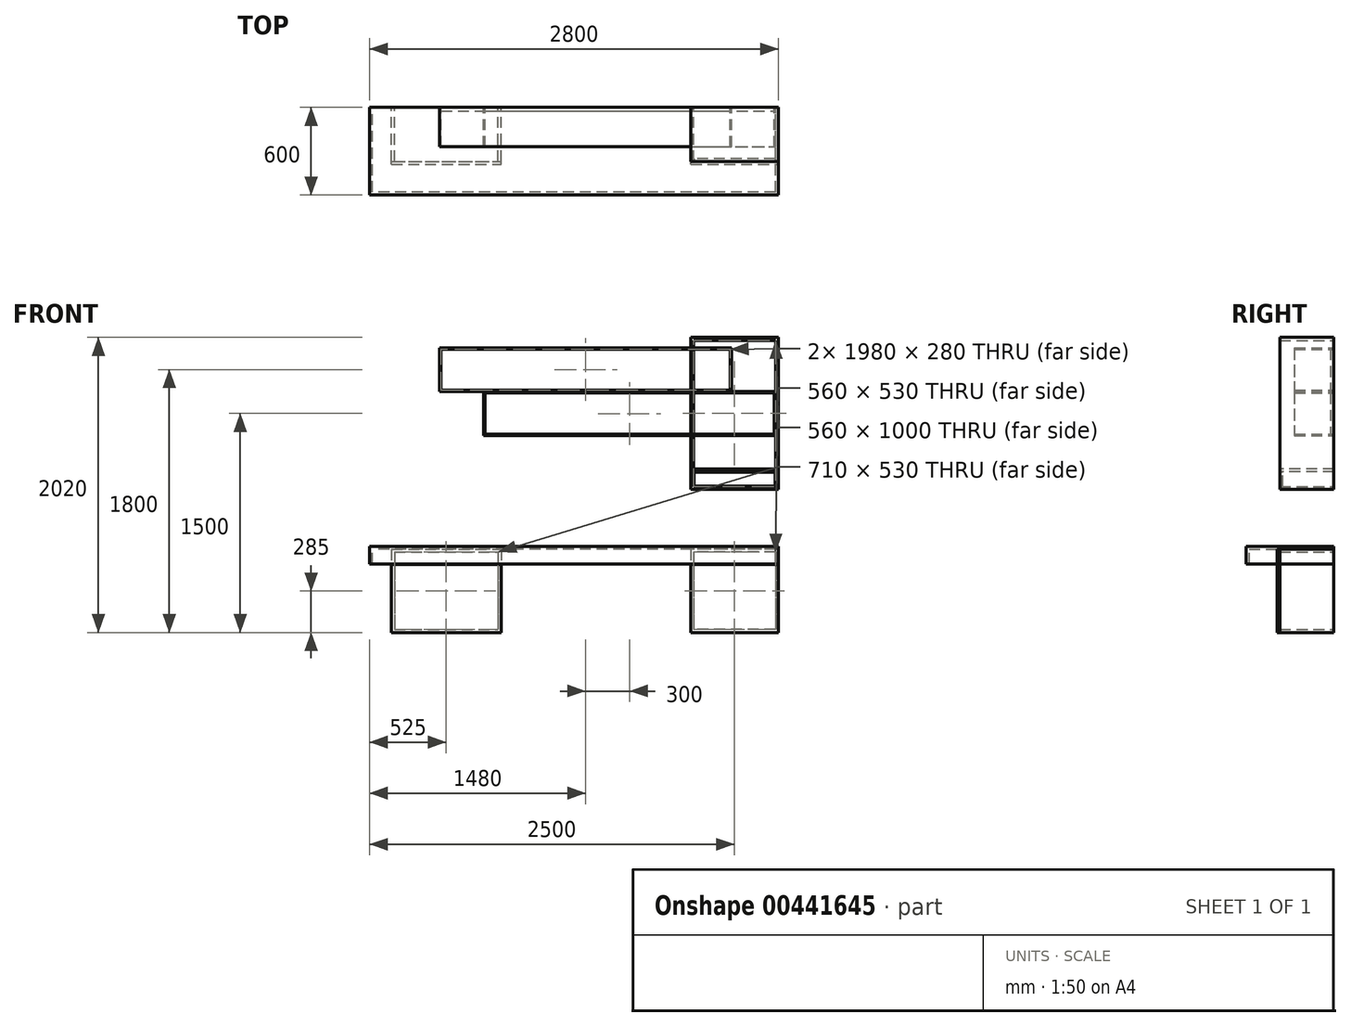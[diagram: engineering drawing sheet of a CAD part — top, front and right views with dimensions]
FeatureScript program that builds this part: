
annotation { "Feature Type Name" : "Feature", "Feature Type Description" : "" }
export const myFeature = defineFeature(function(context is Context, id is Id, definition is map)
    precondition{}
    {
        {
            var Q0;
            Q0=qCreatedBy(makeId("Front.planeOp"),FACE);
            var sketch = newSketch(context, id + "F0", { "sketchPlane" : qUnion([Q0])});
            skLineSegment(sketch, "E0.bottom", {"start": v(-1500, 2200) * mm, "end": v(1500, 2200) * mm});
            skLineSegment(sketch, "E0.top", {"start": v(-1500, 0) * mm, "end": v(1500, 0) * mm});
            skLineSegment(sketch, "E0.left", {"start": v(-1500, 2200) * mm, "end": v(-1500, 0) * mm});
            skLineSegment(sketch, "E0.right", {"start": v(1500, 2200) * mm, "end": v(1500, 0) * mm});
            skPoint(sketch, "E1", {"position": v(0, 0) * mm});
            skLineSegment(sketch, "E2.bottom", {"start": v(-1250, 770) * mm, "end": v(-500, 770) * mm});
            skLineSegment(sketch, "E2.top", {"start": v(-1250, 170) * mm, "end": v(-500, 170) * mm});
            skLineSegment(sketch, "E2.left", {"start": v(-1250, 770) * mm, "end": v(-1250, 170) * mm});
            skLineSegment(sketch, "E2.right", {"start": v(-500, 770) * mm, "end": v(-500, 170) * mm});
            skSolve(sketch);
        }
        {
            var Q0;
            Q0=qCreatedBy(makeId("Top.planeOp"),FACE);
            var Q1;
            Q1=sQuery(id+"F0.wireOp",VERTEX,"E2.left.start");
            cPlane(context, id + "F1", {"entities" : qUnion([Q0, Q1]), "cplaneType" : CPlaneType.PLANE_POINT, "offset" : 25 * mm, "width" : 150 * mm, "height" : 150 * mm});
        }
        {
            var Q0;
            Q0=qCreatedBy(id+"F1.planeOp",FACE);
            var sketch = newSketch(context, id + "F2", { "sketchPlane" : qUnion([Q0])});
            skLineSegment(sketch, "E3.bottom", {"start": v(1400, -600) * mm, "end": v(-1400, -600) * mm});
            skLineSegment(sketch, "E3.top", {"start": v(1400, 0) * mm, "end": v(-1400, 0) * mm});
            skLineSegment(sketch, "E3.left", {"start": v(1400, -600) * mm, "end": v(1400, 0) * mm});
            skLineSegment(sketch, "E3.right", {"start": v(-1400, -600) * mm, "end": v(-1400, 0) * mm});
            skPoint(sketch, "E3.middle", {"position": v(0, -300) * mm});
            skSolve(sketch);
        }
        {
            var Q0;
            Q0=qSketchRegion(id+"F2",true);
            extrude(context, id + "F3", {"entities" : qUnion([Q0]), "depth" : 20 * mm});
        }
        {
            var Q0;
            Q0=makeQuery(id+"F3.opExtrude","CAP_FACE",FACE,{"disambiguationData":[OSD([sQuery(id+"F2.wireOp",EDGE,"E3.bottom"),sQuery(id+"F2.wireOp",EDGE,"E3.top"),sQuery(id+"F2.wireOp",EDGE,"E3.left"),sQuery(id+"F2.wireOp",EDGE,"E3.right")])],"isStart":true});
            var sketch = newSketch(context, id + "F4", { "sketchPlane" : qUnion([Q0])});
            skLineSegment(sketch, "E4.0", {"start": v(-1400, 600) * mm, "end": v(-1400, 0) * mm});
            skLineSegment(sketch, "E4.1", {"start": v(1400, 600) * mm, "end": v(-1400, 600) * mm});
            skLineSegment(sketch, "E4.2", {"start": v(1400, 600) * mm, "end": v(1400, 0) * mm});
            skLineSegment(sketch, "E5.0", {"start": v(-1380, 580) * mm, "end": v(-1380, 0) * mm});
            skLineSegment(sketch, "E5.1", {"start": v(1380, 580) * mm, "end": v(-1380, 580) * mm});
            skLineSegment(sketch, "E5.2", {"start": v(1380, 580) * mm, "end": v(1380, 0) * mm});
            skLineSegment(sketch, "E6", {"start": v(-1400, 0) * mm, "end": v(-1380, 0) * mm});
            skLineSegment(sketch, "E7", {"start": v(1400, 0) * mm, "end": v(1380, 0) * mm});
            skSolve(sketch);
        }
        {
            var Q0;
            Q0=qSketchRegion(id+"F4",true);
            extrude(context, id + "F5", {"entities" : qUnion([Q0]), "operationType" : NewBodyOperationType.ADD, "depth" : 100 * mm});
        }
        {
            var Q0;
            Q0=qCreatedBy(makeId("Front.planeOp"),FACE);
            var sketch = newSketch(context, id + "F6", { "sketchPlane" : qUnion([Q0])});
            skLineSegment(sketch, "E8.bottom", {"start": v(-1250, 770) * mm, "end": v(-500, 770) * mm});
            skLineSegment(sketch, "E8.top", {"start": v(-1250, 200) * mm, "end": v(-500, 200) * mm});
            skLineSegment(sketch, "E8.left", {"start": v(-1250, 770) * mm, "end": v(-1250, 200) * mm});
            skLineSegment(sketch, "E8.right", {"start": v(-500, 770) * mm, "end": v(-500, 200) * mm});
            skLineSegment(sketch, "E9.bottom", {"start": v(1400, 770) * mm, "end": v(800, 770) * mm});
            skLineSegment(sketch, "E9.top", {"start": v(1400, 200) * mm, "end": v(800, 200) * mm});
            skLineSegment(sketch, "E9.left", {"start": v(1400, 770) * mm, "end": v(1400, 200) * mm});
            skLineSegment(sketch, "E9.right", {"start": v(800, 770) * mm, "end": v(800, 200) * mm});
            skLineSegment(sketch, "E10.0", {"start": v(1380, 750) * mm, "end": v(1380, 220) * mm});
            skLineSegment(sketch, "E10.1", {"start": v(1380, 750) * mm, "end": v(820, 750) * mm});
            skLineSegment(sketch, "E10.2", {"start": v(820, 750) * mm, "end": v(820, 220) * mm});
            skLineSegment(sketch, "E10.3", {"start": v(1380, 220) * mm, "end": v(820, 220) * mm});
            skLineSegment(sketch, "E11.0", {"start": v(-1230, 750) * mm, "end": v(-520, 750) * mm});
            skLineSegment(sketch, "E11.1", {"start": v(-1230, 750) * mm, "end": v(-1230, 220) * mm});
            skLineSegment(sketch, "E11.2", {"start": v(-1230, 220) * mm, "end": v(-520, 220) * mm});
            skLineSegment(sketch, "E11.3", {"start": v(-520, 750) * mm, "end": v(-520, 220) * mm});
            skSolve(sketch);
        }
        {
            var Q0;
            Q0=qSketchRegion(id+"F6",true);
            extrude(context, id + "F7", {"entities" : qUnion([Q0]), "depth" : 370 * mm});
        }
        {
            var Q0;
            Q0=makeQuery(id+"F7.opExtrude","CAP_FACE",FACE,{"disambiguationData":[OSD([sQuery(id+"F6.wireOp",EDGE,"E8.bottom"),sQuery(id+"F6.wireOp",EDGE,"E8.top"),sQuery(id+"F6.wireOp",EDGE,"E8.left"),sQuery(id+"F6.wireOp",EDGE,"E8.right"),sQuery(id+"F6.wireOp",EDGE,"E11.0"),sQuery(id+"F6.wireOp",EDGE,"E11.1"),sQuery(id+"F6.wireOp",EDGE,"E11.2"),sQuery(id+"F6.wireOp",EDGE,"E11.3")])],"isStart":false});
            var sketch = newSketch(context, id + "F8", { "sketchPlane" : qUnion([Q0])});
            skLineSegment(sketch, "E12.bottom", {"start": v(-1250, 770) * mm, "end": v(-500, 770) * mm});
            skLineSegment(sketch, "E12.top", {"start": v(-1250, 670) * mm, "end": v(-500, 670) * mm});
            skLineSegment(sketch, "E12.left", {"start": v(-1250, 770) * mm, "end": v(-1250, 670) * mm});
            skLineSegment(sketch, "E12.right", {"start": v(-500, 770) * mm, "end": v(-500, 670) * mm});
            skLineSegment(sketch, "E13.bottom", {"start": v(800, 770) * mm, "end": v(1400, 770) * mm});
            skLineSegment(sketch, "E13.top", {"start": v(800, 670) * mm, "end": v(1400, 670) * mm});
            skLineSegment(sketch, "E13.left", {"start": v(800, 770) * mm, "end": v(800, 670) * mm});
            skLineSegment(sketch, "E13.right", {"start": v(1400, 770) * mm, "end": v(1400, 670) * mm});
            skLineSegment(sketch, "E14.bottom", {"start": v(-1250, 667) * mm, "end": v(-500, 667) * mm});
            skLineSegment(sketch, "E14.top", {"start": v(-1250, 200) * mm, "end": v(-500, 200) * mm});
            skLineSegment(sketch, "E14.left", {"start": v(-1250, 667) * mm, "end": v(-1250, 200) * mm});
            skLineSegment(sketch, "E14.right", {"start": v(-500, 667) * mm, "end": v(-500, 200) * mm});
            skLineSegment(sketch, "E15.bottom", {"start": v(800, 667) * mm, "end": v(1400, 667) * mm});
            skLineSegment(sketch, "E15.top", {"start": v(800, 200) * mm, "end": v(1400, 200) * mm});
            skLineSegment(sketch, "E15.left", {"start": v(800, 667) * mm, "end": v(800, 200) * mm});
            skLineSegment(sketch, "E15.right", {"start": v(1400, 667) * mm, "end": v(1400, 200) * mm});
            skSolve(sketch);
        }
        {
            var Q0;
            Q0=qSketchRegion(id+"F8",true);
            extrude(context, id + "F9", {"entities" : qUnion([Q0]), "depth" : 20 * mm});
        }
        {
            var Q0;
            Q0=makeQuery(id+"F0.imprint","IMPRINT",FACE,{"disambiguationData":[TD([[makeQuery(id+"F0.imprint","IMPRINT",EDGE,{"derivedFrom":sQuery(id+"F0.wireOp",EDGE,"E0.bottom")}),-1.0]])]});
            var sketch = newSketch(context, id + "F10", { "sketchPlane" : qUnion([Q0])});
            skLineSegment(sketch, "E16.bottom", {"start": v(-920, 2150) * mm, "end": v(1080, 2150) * mm});
            skLineSegment(sketch, "E16.top", {"start": v(-920, 1850) * mm, "end": v(1080, 1850) * mm});
            skLineSegment(sketch, "E16.left", {"start": v(-920, 2150) * mm, "end": v(-920, 1850) * mm});
            skLineSegment(sketch, "E16.right", {"start": v(1080, 2150) * mm, "end": v(1080, 1850) * mm});
            skLineSegment(sketch, "E17.bottom", {"start": v(-620, 1849) * mm, "end": v(1380, 1849) * mm});
            skLineSegment(sketch, "E17.top", {"start": v(-620, 1549) * mm, "end": v(1380, 1549) * mm});
            skLineSegment(sketch, "E17.left", {"start": v(-620, 1849) * mm, "end": v(-620, 1549) * mm});
            skLineSegment(sketch, "E17.right", {"start": v(1380, 1849) * mm, "end": v(1380, 1549) * mm});
            skLineSegment(sketch, "E18.0", {"start": v(1070, 2140) * mm, "end": v(1070, 1860) * mm});
            skLineSegment(sketch, "E18.1", {"start": v(-910, 2140) * mm, "end": v(1070, 2140) * mm});
            skLineSegment(sketch, "E18.2", {"start": v(-910, 2140) * mm, "end": v(-910, 1860) * mm});
            skLineSegment(sketch, "E18.3", {"start": v(-910, 1860) * mm, "end": v(1070, 1860) * mm});
            skLineSegment(sketch, "E19.0", {"start": v(1370, 1839) * mm, "end": v(1370, 1559) * mm});
            skLineSegment(sketch, "E19.1", {"start": v(-610, 1839) * mm, "end": v(1370, 1839) * mm});
            skLineSegment(sketch, "E19.2", {"start": v(-610, 1839) * mm, "end": v(-610, 1559) * mm});
            skLineSegment(sketch, "E19.3", {"start": v(-610, 1559) * mm, "end": v(1370, 1559) * mm});
            skSolve(sketch);
        }
        {
            var Q0;
            Q0=qSketchRegion(id+"F10",true);
            extrude(context, id + "F11", {"entities" : qUnion([Q0]), "depth" : 270 * mm});
        }
        {
            var Q0;
            Q0=qCreatedBy(makeId("Front.planeOp"),FACE);
            var sketch = newSketch(context, id + "F12", { "sketchPlane" : qUnion([Q0])});
            skLineSegment(sketch, "E20.0", {"start": v(-910, 2140) * mm, "end": v(-910, 1860) * mm});
            skLineSegment(sketch, "E20.1", {"start": v(-910, 2140) * mm, "end": v(1070, 2140) * mm});
            skLineSegment(sketch, "E20.2", {"start": v(1070, 2140) * mm, "end": v(1070, 1860) * mm});
            skLineSegment(sketch, "E20.3", {"start": v(-910, 1860) * mm, "end": v(1070, 1860) * mm});
            skLineSegment(sketch, "E21.0", {"start": v(-610, 1839) * mm, "end": v(-610, 1559) * mm});
            skLineSegment(sketch, "E21.1", {"start": v(-610, 1839) * mm, "end": v(1370, 1839) * mm});
            skLineSegment(sketch, "E21.2", {"start": v(1370, 1839) * mm, "end": v(1370, 1559) * mm});
            skLineSegment(sketch, "E21.3", {"start": v(-610, 1559) * mm, "end": v(1370, 1559) * mm});
            skSolve(sketch);
        }
        {
            var Q0;
            Q0=qSketchRegion(id+"F12",true);
            extrude(context, id + "F13", {"entities" : qUnion([Q0]), "depth" : 25 * mm});
        }
        {
            var Q0;
            Q0=qCreatedBy(makeId("Front.planeOp"),FACE);
            var sketch = newSketch(context, id + "F14", { "sketchPlane" : qUnion([Q0])});
            skLineSegment(sketch, "E22.bottom", {"start": v(1380, 1200) * mm, "end": v(820, 1200) * mm});
            skLineSegment(sketch, "E22.top", {"start": v(1380, 2200) * mm, "end": v(820, 2200) * mm});
            skLineSegment(sketch, "E22.left", {"start": v(1380, 1200) * mm, "end": v(1380, 2200) * mm});
            skLineSegment(sketch, "E22.right", {"start": v(820, 1200) * mm, "end": v(820, 2200) * mm});
            skLineSegment(sketch, "E23.0", {"start": v(1400, 1180) * mm, "end": v(800, 1180) * mm});
            skLineSegment(sketch, "E23.1", {"start": v(1400, 1180) * mm, "end": v(1400, 2220) * mm});
            skLineSegment(sketch, "E23.2", {"start": v(1400, 2220) * mm, "end": v(800, 2220) * mm});
            skLineSegment(sketch, "E23.3", {"start": v(800, 1180) * mm, "end": v(800, 2220) * mm});
            skSolve(sketch);
        }
        {
            var Q0;
            Q0=qSketchRegion(id+"F14",true);
            extrude(context, id + "F15", {"entities" : qUnion([Q0]), "depth" : 370 * mm});
        }
        {
            var Q0;
            Q0=makeQuery(id+"F15.opExtrude","SWEPT_FACE",FACE,{"disambiguationData":[OSD([sQuery(id+"F14.wireOp",EDGE,"E22.right")])]});
            var sketch = newSketch(context, id + "F16", { "sketchPlane" : qUnion([Q0])});
            skLineSegment(sketch, "E24.bottom", {"start": v(-370, 1320) * mm, "end": v(0, 1320) * mm});
            skLineSegment(sketch, "E24.top", {"start": v(-370, 1300) * mm, "end": v(0, 1300) * mm});
            skLineSegment(sketch, "E24.left", {"start": v(-370, 1320) * mm, "end": v(-370, 1300) * mm});
            skLineSegment(sketch, "E24.right", {"start": v(0, 1320) * mm, "end": v(0, 1300) * mm});
            skSolve(sketch);
        }
        {
            var Q0;
            Q0=qSketchRegion(id+"F16",true);
            extrude(context, id + "F17", {"entities" : qUnion([Q0]), "endBound" : BoundingType.UP_TO_NEXT, "depth" : 25 * mm});
        }
        {
            var Q0;
            Q0=makeQuery(id+"F17.opExtrude","SWEPT_FACE",FACE,{"disambiguationData":[OSD([sQuery(id+"F16.wireOp",EDGE,"E24.left")])]});
            var sketch = newSketch(context, id + "F18", { "sketchPlane" : qUnion([Q0])});
            skLineSegment(sketch, "E25", {"start": v(820, 1300) * mm, "end": v(1380, 1200) * mm, "construction": true});
            skLineSegment(sketch, "E26.bottom", {"start": v(1378, 1202) * mm, "end": v(822, 1202) * mm});
            skLineSegment(sketch, "E26.top", {"start": v(1378, 1298) * mm, "end": v(822, 1298) * mm});
            skLineSegment(sketch, "E26.left", {"start": v(1378, 1202) * mm, "end": v(1378, 1298) * mm});
            skLineSegment(sketch, "E26.right", {"start": v(822, 1202) * mm, "end": v(822, 1298) * mm});
            skPoint(sketch, "E26.middle", {"position": v(1100, 1250) * mm});
            skSolve(sketch);
        }
        {
            var Q0;
            Q0=qSketchRegion(id+"F18",true);
            extrude(context, id + "F19", {"entities" : qUnion([Q0]), "oppositeDirection" : true, "depth" : 20 * mm});
        }
    });
